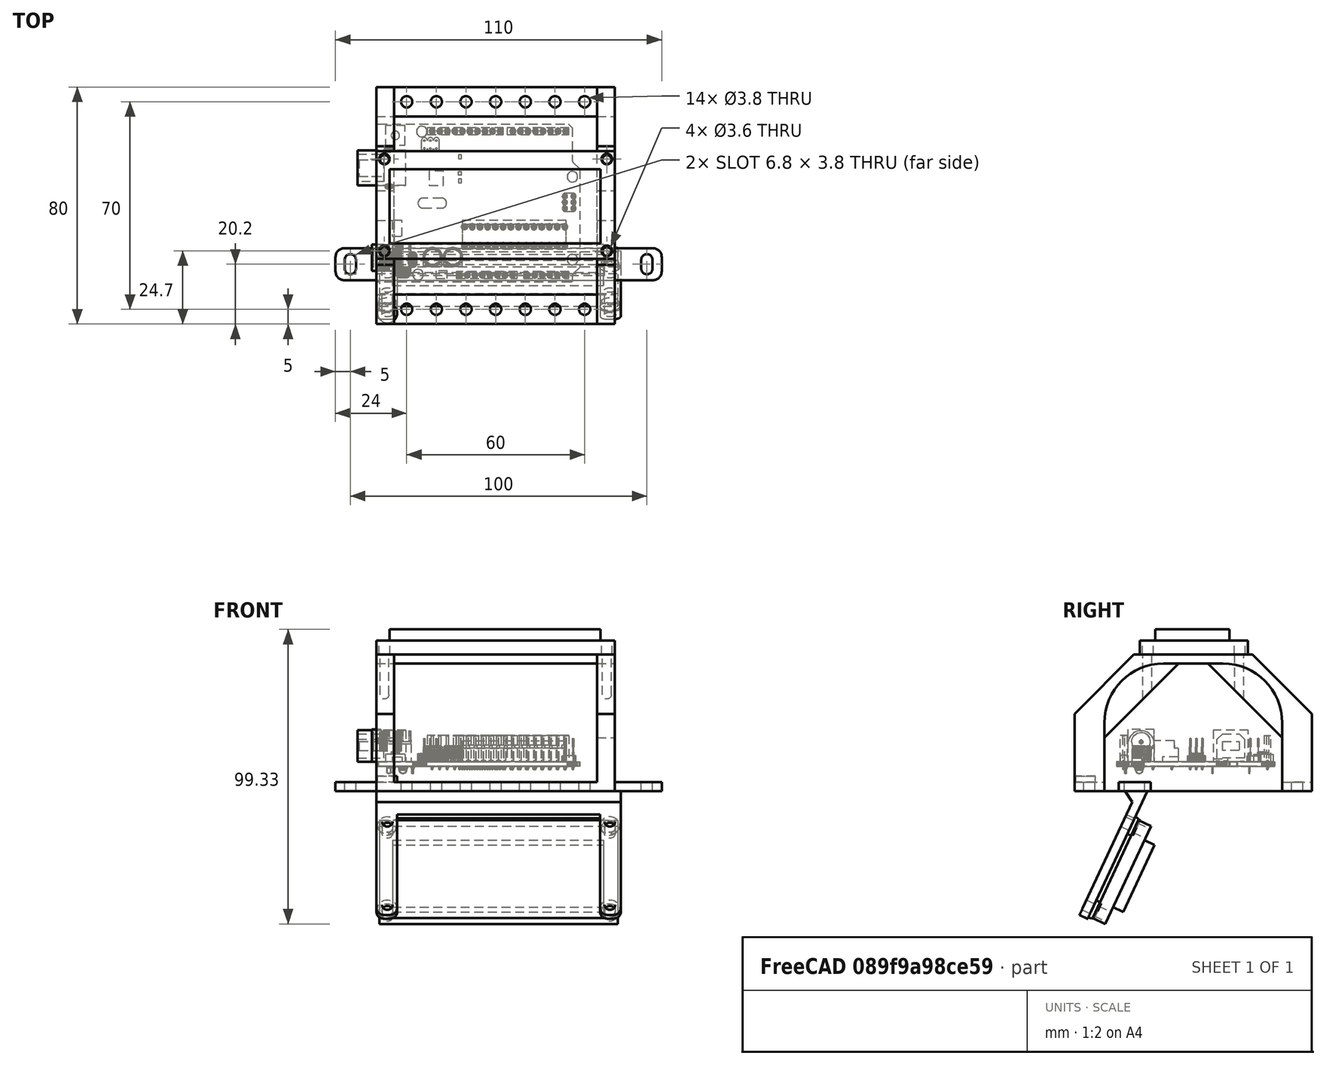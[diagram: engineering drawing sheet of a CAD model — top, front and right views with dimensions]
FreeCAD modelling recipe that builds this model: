
FCSTD DOCUMENT  (FreeCAD 0.18.4R)
Label: 16x2lcd
License: FreeArt
LicenseURL: http://artlibre.org/licence/lal
objects: Part::Box×8, Part::MultiFuse×5, Part::Cylinder×4, Part::FeaturePython×4, Part::Cut×3, Part::Chamfer×3, PartDesign::FeatureBase×3, PartDesign::Body×3, Part::Fillet×2, Part::Feature×2, Spreadsheet::Sheet×1, Part::Cone×1, App::Part×1, Part::Compound×1
note: 39 computed .brp shape members not serialized (recipe doc carries the construction recipe); baked Part::Feature solids carry a one-line shape summary decoded from their .brp

FEATURE [Spreadsheet::Sheet] Spreadsheet  label="p"
  cells = A1=pcb_x; B1(pcb_x)=80.40000000000001; A2=pcb_y; B2(pcb_y)=36.4; A3=pcb_z; B3(pcb_z)=1.7; A4=hole_dist_x; B4(hole_dist_x)=75; A5=hole_dist_y; B5(hole_dist_y)=31; A6=side_wall; B6(side_wall)=1; A7=back_bottom_extra; B7(back_bottom_extra)=10; A8=bolt_hole_stand_wall; B8(bolt_hole_stand_wall)=1.5; A9=bolt_hole_stand_z; B9(bolt_hole_stand_z)=2; A10=bolt_hole_r; B10(bolt_hole_r)=1.8; A11=holder_width; B11(holder_width)=6; A12=back_wall; B12(back_wall)=3; A13=lcd_display_x; B13(lcd_display_x)=71.2; A14=lcd_display_y; B14(lcd_display_y)=25; A15=lcd_display_z; B15(lcd_display_z)=3.8; A17=attach_hole_dist; B17(attach_hole_dist)=10; A18=attach_hole_r; B18(attach_hole_r)=1.9; A19=attach_z; B19(attach_z)=3; A20=attach_width; B20(attach_width)=10; A22=uno_space_x; B22(uno_space_x)=69; A23=uno_space_y; B23(uno_space_y)=60; A24=uno_space_z; B24(uno_space_z)=43; A25=screw_hole_r; B25(screw_hole_r)=1.5
FEATURE [Part::Box] Box006  label="lcd back holder"
  AttacherType = Attacher::AttachEngine3D
  Height = 3
  Length = 82.4
  Placement = pos=(0,-10,0) rot=(0,0,1;0rad)
  Width = 48.4
  expr: Placement.Base.y = -p.back_bottom_extra
  expr: Width = 2 * p.side_wall + p.pcb_y + p.back_bottom_extra
  expr: Height = p.back_wall
  expr: Length = 2 * p.side_wall + p.pcb_x
FEATURE [Part::Cylinder] Cylinder002  label="hole001"
  Angle = 360
  AttacherType = Attacher::AttachEngine3D
  Height = 10
  Placement = pos=(3.7,3.7,0) rot=(0,0,1;0rad)
  Radius = 1.8
  expr: Placement.Base.y = (2 * p.side_wall + p.pcb_y - p.hole_dist_y) / 2
  expr: Placement.Base.x = (2 * p.side_wall + p.pcb_x - p.hole_dist_x) / 2
  expr: Radius = p.bolt_hole_r
FEATURE [Part::FeaturePython] Array003  label="hole array001"  # Draft array (typed FeaturePython)
  Angle = 360
  ArrayType = 0
  Axis = (0,0,1)
  Base = -> Cylinder002
  Center = (0,0,0)
  Fuse = false
  IntervalAxis = (0,0,0)
  IntervalX = (75,0,0)
  IntervalY = (0,31,0)
  IntervalZ = (0,0,1)
  NumberPolar = 1
  NumberX = 2
  NumberY = 2
  NumberZ = 1
  expr: IntervalY.y = p.hole_dist_y
  expr: IntervalX.x = p.hole_dist_x
FEATURE [Part::Box] Box007  label="lcd back holder extraction"
  AttacherType = Attacher::AttachEngine3D
  Height = 3
  Length = 68.4
  Placement = pos=(7,1,0) rot=(0,0,1;0rad)
  Width = 72.8
  expr: Placement.Base.y = p.side_wall
  expr: Placement.Base.x = p.side_wall + p.holder_width
  expr: Width = p.pcb_y * 2 * p.side_wall
  expr: Height = p.back_wall
  expr: Length = p.pcb_x - 2 * p.holder_width
FEATURE [Part::MultiFuse] Fusion002  label="back extraction fusion"
  Shapes = -> [Array003,Box007]
FEATURE [Part::Cylinder] Cylinder  label="hole stand"
  Angle = 360
  AttacherType = Attacher::AttachEngine3D
  Height = 2
  Placement = pos=(3.7,3.7,3) rot=(0,0,1;0rad)
  Radius = 3.3
  expr: Placement.Base.z = p.back_wall
  expr: Placement.Base.y = (2 * p.side_wall + p.pcb_y - p.hole_dist_y) / 2
  expr: Placement.Base.x = (2 * p.side_wall + p.pcb_x - p.hole_dist_x) / 2
  expr: Radius = p.bolt_hole_r + p.bolt_hole_stand_wall
FEATURE [Part::Cone] Cone  label="hole stand cone"
  Angle = 360
  AttacherType = Attacher::AttachEngine3D
  Height = 2
  Placement = pos=(3.7,3.7,3) rot=(0,0,1;0rad)
  Radius1 = 3.3
  Radius2 = 2.8
  expr: Height = p.bolt_hole_stand_z
  expr: Placement.Base.z = p.back_wall
  expr: Placement.Base.y = (2 * p.side_wall + p.pcb_y - p.hole_dist_y) / 2
  expr: Placement.Base.x = (2 * p.side_wall + p.pcb_x - p.hole_dist_x) / 2
  expr: Radius2 = p.bolt_hole_r + p.bolt_hole_stand_wall - 0.5
  expr: Radius1 = p.bolt_hole_r + p.bolt_hole_stand_wall
FEATURE [Part::FeaturePython] Array004  label="hole array002"  # Draft array (typed FeaturePython)
  Angle = 360
  ArrayType = 0
  Axis = (0,0,1)
  Base = -> Cone
  Center = (0,0,0)
  Fuse = false
  IntervalAxis = (0,0,0)
  IntervalX = (75,0,0)
  IntervalY = (0,31,0)
  IntervalZ = (0,0,1)
  NumberPolar = 1
  NumberX = 2
  NumberY = 2
  NumberZ = 1
  expr: IntervalY.y = p.hole_dist_y
  expr: IntervalX.x = p.hole_dist_x
FEATURE [Part::MultiFuse] Fusion  label="lcd back holder fusion"
  Shapes = -> [Box006,Array004]
FEATURE [Part::Cut] Cut003  label="back cut"
  Base = -> Fusion
  Tool = -> Fusion002
FEATURE [Part::Fillet] Fillet003  label="back cut fillet"
  Base = -> Cut003
  Edges = 4 edges r=2.5: [Edge3,Edge25,Edge35,Edge38]
  Placement = pos=(0,17.89,-6.98) rot=(-1,0,0;2.00713rad)
FEATURE [Part::Box] Box  label="display cube"
  AttacherType = Attacher::AttachEngine3D
  Height = 3.8
  Length = 71.2
  Placement = pos=(4.4,5.2,4.7) rot=(0,0,1;0rad)
  Width = 25
  expr: Width = p.lcd_display_y
  expr: Length = p.lcd_display_x
  expr: Placement.Base.x = (p.pcb_x - p.lcd_display_x) / 2 - 0.2
  expr: Placement.Base.y = (p.pcb_y - p.lcd_display_y) / 2 - 0.5
  expr: Height = p.lcd_display_z
  expr: Placement.Base.z = p.pcb_z + 3
FEATURE [Part::Box] Box008  label="under display"
  AttacherType = Attacher::AttachEngine3D
  Height = 4.7
  Length = 80.4
  Width = 36.4
  expr: Height = p.pcb_z + 3
  expr: Width = p.pcb_y
  expr: Length = p.pcb_x
FEATURE [Part::Feature] Cut003001  label="attach plane x dir001"
  Placement = pos=(1,2,0) rot=(0,0,1;0rad)
  shape: bbox 110 x 10.8 x 3 mm, 18 faces (baked)
FEATURE [Part::MultiFuse] Fusion003  label="back holder fusion"
  Shapes = -> [Fillet003,Cut003001]
FEATURE [Part::Chamfer] Chamfer  label="lcd back holder chamber"
  Base = -> Fusion003
  Edges = 1 edges r=4.1: [Edge37]
FEATURE [PartDesign::FeatureBase] Clone
  BaseFeature = -> Array003
FEATURE [PartDesign::Body] Body  label="hole clone"
  BaseFeature = -> Array003
  Group = -> [Clone]
  Origin = -> Origin001
  Placement = pos=(-1,-1,0) rot=(0,0,1;0rad)
  Tip = -> Clone
  expr: Placement.Base.y = -p.side_wall
  expr: Placement.Base.x = -p.side_wall
FEATURE [Part::MultiFuse] Fusion004  label="lcd fusion"
  Shapes = -> [Box,Box008]
FEATURE [Part::Cut] Cut  label="lcd cut"
  Base = -> Fusion004
  Tool = -> Body
FEATURE [App::Part] Part  label="16x2 lcd mockup"
  Group = -> [Box,Box008,Fusion004,Body,Cut]
  Origin = -> Origin
FEATURE [PartDesign::FeatureBase] Clone001
  BaseFeature = -> Cut
FEATURE [PartDesign::Body] Body001  label="16x2 lcd clone"
  BaseFeature = -> Cut
  Group = -> [Clone001]
  Origin = -> Origin002
  Placement = pos=(1,21.4606,-9.85574) rot=(-1,0,0;2.00713rad)
  Tip = -> Clone001
FEATURE [Part::Compound] Compound  label="16x2 lcd compound"
  Links = -> [Chamfer,Body001]
FEATURE [Part::Box] Box009  label="v cube"
  AttacherType = Attacher::AttachEngine3D
  Height = 46
  Length = 80.4
  Width = 80
  expr: Height = p.uno_space_z + p.back_wall
  expr: Width = p.uno_space_y + 2 * p.attach_width
  expr: Length = p.pcb_x
FEATURE [Part::Box] Box010  label="v cube extract"
  AttacherType = Attacher::AttachEngine3D
  Height = 43
  Length = 80.4
  Placement = pos=(0,10,0) rot=(0,0,1;0rad)
  Width = 60
  expr: Placement.Base.y = p.attach_width
  expr: Height = p.uno_space_z
  expr: Width = p.uno_space_y
  expr: Length = p.pcb_x
FEATURE [Part::Box] Box011  label="v cube middle extract"
  AttacherType = Attacher::AttachEngine3D
  Height = 40
  Length = 68.4
  Placement = pos=(6,0,3) rot=(0,0,1;0rad)
  Width = 80
  expr: Placement.Base.x = p.holder_width
  expr: Placement.Base.z = p.attach_z
  expr: Height = p.uno_space_z - p.attach_z
  expr: Width = p.uno_space_y + 2 * p.attach_width
  expr: Length = p.pcb_x - 2 * p.holder_width
FEATURE [PartDesign::FeatureBase] Clone002
  BaseFeature = -> Cut
FEATURE [PartDesign::Body] Body002  label="16x2 lcd mockup clone"
  Group = -> [Clone002]
  Origin = -> Origin003
  Placement = pos=(0,22,46) rot=(0,0,1;0rad)
  Tip = -> Clone002
FEATURE [Part::Box] Box012  label="v cube extract001"
  AttacherType = Attacher::AttachEngine3D
  Height = 43
  Length = 68.4
  Placement = pos=(6,0,3) rot=(0,0,1;0rad)
  Width = 80
  expr: Placement.Base.x = p.holder_width
  expr: Placement.Base.z = p.attach_z
  expr: Height = p.uno_space_z
  expr: Width = p.uno_space_y + 2 * p.attach_width
  expr: Length = p.pcb_x - 2 * p.holder_width
FEATURE [Part::Cylinder] Cylinder003  label="screw hole"
  Angle = 360
  AttacherType = Attacher::AttachEngine3D
  Height = 50
  Placement = pos=(0,0,-40) rot=(0,0,1;0rad)
  Radius = 1.5
  expr: Radius = p.screw_hole_r
FEATURE [Part::FeaturePython] Array005  label="screw hole array"  # Draft array (typed FeaturePython)
  Angle = 360
  ArrayType = 0
  Axis = (0,0,1)
  Base = -> Cylinder003
  Center = (0,0,0)
  Fuse = false
  IntervalAxis = (0,0,0)
  IntervalX = (75,0,0)
  IntervalY = (0,31,0)
  IntervalZ = (0,0,1)
  NumberPolar = 1
  NumberX = 2
  NumberY = 2
  NumberZ = 1
  Placement = pos=(2.7,24.5,43) rot=(0,0,1;0rad)
  expr: Placement.Base.z = p.uno_space_z
  expr: Placement.Base.x = (p.pcb_x - p.hole_dist_x) / 2
  expr: Placement.Base.y = (p.uno_space_y + 2 * p.attach_width - p.hole_dist_y) / 2
  expr: IntervalY.y = p.hole_dist_y
  expr: IntervalX.x = p.hole_dist_x
FEATURE [Part::Cylinder] Cylinder004  label="attachment hole"
  Angle = 360
  AttacherType = Attacher::AttachEngine3D
  Height = 10
  Radius = 1.9
  expr: Radius = p.attach_hole_r
FEATURE [Part::FeaturePython] Array  label="attachment hole array"  # Draft array (typed FeaturePython)
  Angle = 360
  ArrayType = 0
  Axis = (0,0,1)
  Base = -> Cylinder004
  Center = (0,0,0)
  Fuse = false
  IntervalAxis = (0,0,0)
  IntervalX = (10,0,0)
  IntervalY = (0,10,0)
  IntervalZ = (0,0,1)
  NumberPolar = 1
  NumberX = 7
  NumberY = 8
  NumberZ = 1
  Placement = pos=(10.2,5,0) rot=(0,0,1;0rad)
  expr: Placement.Base.y = p.attach_width / 2
  expr: Placement.Base.x = (p.pcb_x - (NumberX - 1) * p.attach_hole_dist) / 2
  expr: NumberX = (p.pcb_x - 2 * p.holder_width) / p.attach_hole_dist
  expr: NumberY = (p.uno_space_y + 2 * p.attach_width) / p.attach_hole_dist
  expr: IntervalY.y = p.attach_hole_dist
  expr: IntervalX.x = p.attach_hole_dist
FEATURE [Part::Feature] Solid  label="Arduino"
  Placement = pos=(26.2,5.9,40) rot=(0,0,-1;1.5708rad)
  shape: large baked B-rep (35 MB .brp); summary skipped
FEATURE [Part::Fillet] Fillet  label="v cube extract fillet"
  Base = -> Box010
  Edges = 2 edges r=20: [Edge10,Edge12]
FEATURE [Part::Chamfer] Chamfer001  label="v cube extract chamfer"
  Base = -> Box010
  Edges = 2 edges r=25: [Edge10,Edge12]
FEATURE [Part::MultiFuse] Fusion005  label="v extract union"
  Shapes = -> [Box011,Box012,Array005,Array,Chamfer001]
FEATURE [Part::Chamfer] Chamfer002  label="v cube chamfer"
  Base = -> Box009
  Edges = 2 edges r=20: [Edge10,Edge12]
FEATURE [Part::Cut] Cut003002  label="v cut"
  Base = -> Chamfer002
  Tool = -> Fusion005
